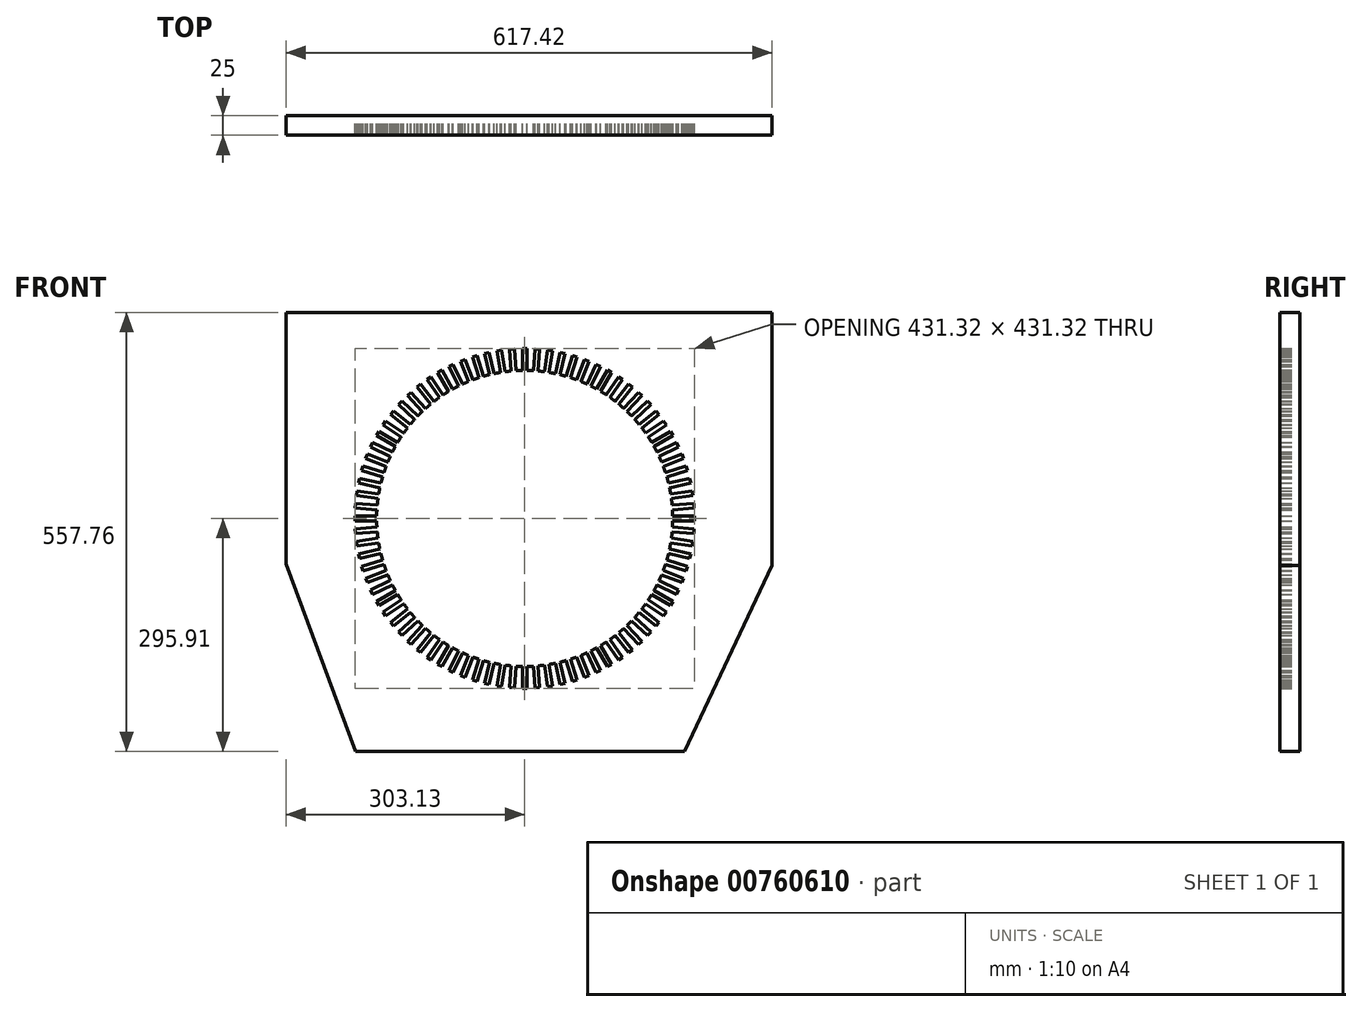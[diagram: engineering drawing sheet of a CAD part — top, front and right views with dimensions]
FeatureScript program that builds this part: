
annotation { "Feature Type Name" : "Feature", "Feature Type Description" : "" }
export const myFeature = defineFeature(function(context is Context, id is Id, definition is map)
    precondition{}
    {
        {
            var Q0;
            Q0=qCreatedBy(makeId("Front.planeOp"),FACE);
            var sketch = newSketch(context, id + "F0", { "sketchPlane" : qUnion([Q0])});
            skCircle(sketch, "E0", {"center": v(0, 0) * mm, "radius": 188.04 * mm});
            skLineSegment(sketch, "E1.top", {"start": v(3, 215.66) * mm, "end": v(-3, 215.66) * mm});
            skLineSegment(sketch, "E1.left", {"start": v(3, 185.67) * mm, "end": v(3, 215.66) * mm});
            skLineSegment(sketch, "E1.right", {"start": v(-3, 185.67) * mm, "end": v(-3, 215.66) * mm});
            skPoint(sketch, "E1.middle", {"position": v(0, 200.67) * mm});
            skLineSegment(sketch, "E2", {"start": v(0, 184.62) * mm, "end": v(0, -162.33) * mm, "construction": true});
            skLineSegment(sketch, "E3.1.0", {"start": v(-10.88, 185.38) * mm, "end": v(-13.12, 215.28) * mm});
            skLineSegment(sketch, "E3.1.1", {"start": v(-16.87, 184.93) * mm, "end": v(-19.1, 214.83) * mm});
            skPoint(sketch, "E3.1.2", {"position": v(-15, 200.1) * mm});
            skLineSegment(sketch, "E3.1.3", {"start": v(-13.12, 215.28) * mm, "end": v(-19.1, 214.83) * mm});
            skLineSegment(sketch, "E3.2.0", {"start": v(-24.7, 184.05) * mm, "end": v(-29.18, 213.7) * mm});
            skLineSegment(sketch, "E3.2.1", {"start": v(-30.64, 183.15) * mm, "end": v(-35.1, 212.8) * mm});
            skPoint(sketch, "E3.2.2", {"position": v(-29.9, 198.43) * mm});
            skLineSegment(sketch, "E3.2.3", {"start": v(-29.18, 213.7) * mm, "end": v(-35.1, 212.8) * mm});
            skLineSegment(sketch, "E3.3.0", {"start": v(-38.4, 181.69) * mm, "end": v(-45.06, 210.92) * mm});
            skLineSegment(sketch, "E3.3.1", {"start": v(-44.24, 180.35) * mm, "end": v(-50.91, 209.59) * mm});
            skPoint(sketch, "E3.3.2", {"position": v(-44.65, 195.64) * mm});
            skLineSegment(sketch, "E3.3.3", {"start": v(-45.06, 210.92) * mm, "end": v(-50.91, 209.59) * mm});
            skLineSegment(sketch, "E3.4.0", {"start": v(-51.86, 178.3) * mm, "end": v(-60.7, 206.96) * mm});
            skLineSegment(sketch, "E3.4.1", {"start": v(-57.6, 176.54) * mm, "end": v(-66.43, 205.2) * mm});
            skPoint(sketch, "E3.4.2", {"position": v(-59.15, 191.75) * mm});
            skLineSegment(sketch, "E3.4.3", {"start": v(-60.7, 206.96) * mm, "end": v(-66.43, 205.2) * mm});
            skLineSegment(sketch, "E3.5.0", {"start": v(-65.04, 173.93) * mm, "end": v(-76, 201.85) * mm});
            skLineSegment(sketch, "E3.5.1", {"start": v(-70.63, 171.74) * mm, "end": v(-81.58, 199.66) * mm});
            skPoint(sketch, "E3.5.2", {"position": v(-73.31, 186.8) * mm});
            skLineSegment(sketch, "E3.5.3", {"start": v(-76, 201.85) * mm, "end": v(-81.58, 199.66) * mm});
            skLineSegment(sketch, "E3.6.0", {"start": v(-77.86, 168.59) * mm, "end": v(-90.87, 195.6) * mm});
            skLineSegment(sketch, "E3.6.1", {"start": v(-83.26, 165.98) * mm, "end": v(-96.27, 193) * mm});
            skPoint(sketch, "E3.6.2", {"position": v(-87.07, 180.8) * mm});
            skLineSegment(sketch, "E3.6.3", {"start": v(-90.87, 195.6) * mm, "end": v(-96.27, 193) * mm});
            skLineSegment(sketch, "E3.7.0", {"start": v(-90.24, 162.3) * mm, "end": v(-105.23, 188.27) * mm});
            skLineSegment(sketch, "E3.7.1", {"start": v(-95.43, 159.3) * mm, "end": v(-110.43, 185.27) * mm});
            skPoint(sketch, "E3.7.2", {"position": v(-100.33, 173.78) * mm});
            skLineSegment(sketch, "E3.7.3", {"start": v(-105.23, 188.27) * mm, "end": v(-110.43, 185.27) * mm});
            skLineSegment(sketch, "E3.8.0", {"start": v(-102.11, 155.1) * mm, "end": v(-119, 179.88) * mm});
            skLineSegment(sketch, "E3.8.1", {"start": v(-107.07, 151.72) * mm, "end": v(-123.96, 176.5) * mm});
            skPoint(sketch, "E3.8.2", {"position": v(-113.04, 165.8) * mm});
            skLineSegment(sketch, "E3.8.3", {"start": v(-119, 179.88) * mm, "end": v(-123.96, 176.5) * mm});
            skLineSegment(sketch, "E3.9.0", {"start": v(-113.42, 147.04) * mm, "end": v(-132.12, 170.48) * mm});
            skLineSegment(sketch, "E3.9.1", {"start": v(-118.11, 143.3) * mm, "end": v(-136.8, 166.74) * mm});
            skPoint(sketch, "E3.9.2", {"position": v(-125.11, 156.89) * mm});
            skLineSegment(sketch, "E3.9.3", {"start": v(-132.12, 170.48) * mm, "end": v(-136.8, 166.74) * mm});
            skLineSegment(sketch, "E3.10.0", {"start": v(-124.1, 138.15) * mm, "end": v(-144.49, 160.13) * mm});
            skLineSegment(sketch, "E3.10.1", {"start": v(-128.49, 134.07) * mm, "end": v(-148.89, 156.05) * mm});
            skPoint(sketch, "E3.10.2", {"position": v(-136.49, 147.1) * mm});
            skLineSegment(sketch, "E3.10.3", {"start": v(-144.49, 160.13) * mm, "end": v(-148.89, 156.05) * mm});
            skLineSegment(sketch, "E3.11.0", {"start": v(-134.07, 128.49) * mm, "end": v(-156.05, 148.89) * mm});
            skLineSegment(sketch, "E3.11.1", {"start": v(-138.15, 124.1) * mm, "end": v(-160.13, 144.49) * mm});
            skPoint(sketch, "E3.11.2", {"position": v(-147.1, 136.49) * mm});
            skLineSegment(sketch, "E3.11.3", {"start": v(-156.05, 148.89) * mm, "end": v(-160.13, 144.49) * mm});
            skLineSegment(sketch, "E3.12.0", {"start": v(-143.3, 118.11) * mm, "end": v(-166.74, 136.8) * mm});
            skLineSegment(sketch, "E3.12.1", {"start": v(-147.04, 113.42) * mm, "end": v(-170.48, 132.12) * mm});
            skPoint(sketch, "E3.12.2", {"position": v(-156.89, 125.11) * mm});
            skLineSegment(sketch, "E3.12.3", {"start": v(-166.74, 136.8) * mm, "end": v(-170.48, 132.12) * mm});
            skLineSegment(sketch, "E3.13.0", {"start": v(-151.72, 107.07) * mm, "end": v(-176.5, 123.96) * mm});
            skLineSegment(sketch, "E3.13.1", {"start": v(-155.1, 102.11) * mm, "end": v(-179.88, 119) * mm});
            skPoint(sketch, "E3.13.2", {"position": v(-165.8, 113.04) * mm});
            skLineSegment(sketch, "E3.13.3", {"start": v(-176.5, 123.96) * mm, "end": v(-179.88, 119) * mm});
            skLineSegment(sketch, "E3.14.0", {"start": v(-159.3, 95.43) * mm, "end": v(-185.27, 110.43) * mm});
            skLineSegment(sketch, "E3.14.1", {"start": v(-162.3, 90.24) * mm, "end": v(-188.27, 105.23) * mm});
            skPoint(sketch, "E3.14.2", {"position": v(-173.78, 100.33) * mm});
            skLineSegment(sketch, "E3.14.3", {"start": v(-185.27, 110.43) * mm, "end": v(-188.27, 105.23) * mm});
            skLineSegment(sketch, "E3.15.0", {"start": v(-165.98, 83.26) * mm, "end": v(-193, 96.27) * mm});
            skLineSegment(sketch, "E3.15.1", {"start": v(-168.59, 77.86) * mm, "end": v(-195.6, 90.87) * mm});
            skPoint(sketch, "E3.15.2", {"position": v(-180.8, 87.07) * mm});
            skLineSegment(sketch, "E3.15.3", {"start": v(-193, 96.27) * mm, "end": v(-195.6, 90.87) * mm});
            skLineSegment(sketch, "E3.16.0", {"start": v(-171.74, 70.63) * mm, "end": v(-199.66, 81.58) * mm});
            skLineSegment(sketch, "E3.16.1", {"start": v(-173.93, 65.04) * mm, "end": v(-201.85, 76) * mm});
            skPoint(sketch, "E3.16.2", {"position": v(-186.8, 73.31) * mm});
            skLineSegment(sketch, "E3.16.3", {"start": v(-199.66, 81.58) * mm, "end": v(-201.85, 76) * mm});
            skLineSegment(sketch, "E3.17.0", {"start": v(-176.54, 57.6) * mm, "end": v(-205.2, 66.43) * mm});
            skLineSegment(sketch, "E3.17.1", {"start": v(-178.3, 51.86) * mm, "end": v(-206.96, 60.7) * mm});
            skPoint(sketch, "E3.17.2", {"position": v(-191.75, 59.15) * mm});
            skLineSegment(sketch, "E3.17.3", {"start": v(-205.2, 66.43) * mm, "end": v(-206.96, 60.7) * mm});
            skLineSegment(sketch, "E3.18.0", {"start": v(-180.35, 44.24) * mm, "end": v(-209.59, 50.91) * mm});
            skLineSegment(sketch, "E3.18.1", {"start": v(-181.69, 38.4) * mm, "end": v(-210.92, 45.06) * mm});
            skPoint(sketch, "E3.18.2", {"position": v(-195.64, 44.65) * mm});
            skLineSegment(sketch, "E3.18.3", {"start": v(-209.59, 50.91) * mm, "end": v(-210.92, 45.06) * mm});
            skLineSegment(sketch, "E3.19.0", {"start": v(-183.15, 30.64) * mm, "end": v(-212.8, 35.1) * mm});
            skLineSegment(sketch, "E3.19.1", {"start": v(-184.05, 24.7) * mm, "end": v(-213.7, 29.18) * mm});
            skPoint(sketch, "E3.19.2", {"position": v(-198.43, 29.9) * mm});
            skLineSegment(sketch, "E3.19.3", {"start": v(-212.8, 35.1) * mm, "end": v(-213.7, 29.18) * mm});
            skLineSegment(sketch, "E3.20.0", {"start": v(-184.93, 16.87) * mm, "end": v(-214.83, 19.1) * mm});
            skLineSegment(sketch, "E3.20.1", {"start": v(-185.38, 10.88) * mm, "end": v(-215.28, 13.12) * mm});
            skPoint(sketch, "E3.20.2", {"position": v(-200.1, 15) * mm});
            skLineSegment(sketch, "E3.20.3", {"start": v(-214.83, 19.1) * mm, "end": v(-215.28, 13.12) * mm});
            skLineSegment(sketch, "E3.21.0", {"start": v(-185.67, 3) * mm, "end": v(-215.66, 3) * mm});
            skLineSegment(sketch, "E3.21.1", {"start": v(-185.67, -3) * mm, "end": v(-215.66, -3) * mm});
            skPoint(sketch, "E3.21.2", {"position": v(-200.67, 0) * mm});
            skLineSegment(sketch, "E3.21.3", {"start": v(-215.66, 3) * mm, "end": v(-215.66, -3) * mm});
            skLineSegment(sketch, "E3.22.0", {"start": v(-185.38, -10.88) * mm, "end": v(-215.28, -13.12) * mm});
            skLineSegment(sketch, "E3.22.1", {"start": v(-184.93, -16.87) * mm, "end": v(-214.83, -19.1) * mm});
            skPoint(sketch, "E3.22.2", {"position": v(-200.1, -15) * mm});
            skLineSegment(sketch, "E3.22.3", {"start": v(-215.28, -13.12) * mm, "end": v(-214.83, -19.1) * mm});
            skLineSegment(sketch, "E3.23.0", {"start": v(-184.05, -24.7) * mm, "end": v(-213.7, -29.18) * mm});
            skLineSegment(sketch, "E3.23.1", {"start": v(-183.15, -30.64) * mm, "end": v(-212.8, -35.1) * mm});
            skPoint(sketch, "E3.23.2", {"position": v(-198.43, -29.9) * mm});
            skLineSegment(sketch, "E3.23.3", {"start": v(-213.7, -29.18) * mm, "end": v(-212.8, -35.1) * mm});
            skLineSegment(sketch, "E3.24.0", {"start": v(-181.69, -38.4) * mm, "end": v(-210.92, -45.06) * mm});
            skLineSegment(sketch, "E3.24.1", {"start": v(-180.35, -44.24) * mm, "end": v(-209.59, -50.91) * mm});
            skPoint(sketch, "E3.24.2", {"position": v(-195.64, -44.65) * mm});
            skLineSegment(sketch, "E3.24.3", {"start": v(-210.92, -45.06) * mm, "end": v(-209.59, -50.91) * mm});
            skLineSegment(sketch, "E3.25.0", {"start": v(-178.3, -51.86) * mm, "end": v(-206.96, -60.7) * mm});
            skLineSegment(sketch, "E3.25.1", {"start": v(-176.54, -57.6) * mm, "end": v(-205.2, -66.43) * mm});
            skPoint(sketch, "E3.25.2", {"position": v(-191.75, -59.15) * mm});
            skLineSegment(sketch, "E3.25.3", {"start": v(-206.96, -60.7) * mm, "end": v(-205.2, -66.43) * mm});
            skLineSegment(sketch, "E3.26.0", {"start": v(-173.93, -65.04) * mm, "end": v(-201.85, -76) * mm});
            skLineSegment(sketch, "E3.26.1", {"start": v(-171.74, -70.63) * mm, "end": v(-199.66, -81.58) * mm});
            skPoint(sketch, "E3.26.2", {"position": v(-186.8, -73.31) * mm});
            skLineSegment(sketch, "E3.26.3", {"start": v(-201.85, -76) * mm, "end": v(-199.66, -81.58) * mm});
            skLineSegment(sketch, "E3.27.0", {"start": v(-168.59, -77.86) * mm, "end": v(-195.6, -90.87) * mm});
            skLineSegment(sketch, "E3.27.1", {"start": v(-165.98, -83.26) * mm, "end": v(-193, -96.27) * mm});
            skPoint(sketch, "E3.27.2", {"position": v(-180.8, -87.07) * mm});
            skLineSegment(sketch, "E3.27.3", {"start": v(-195.6, -90.87) * mm, "end": v(-193, -96.27) * mm});
            skLineSegment(sketch, "E3.28.0", {"start": v(-162.3, -90.24) * mm, "end": v(-188.27, -105.23) * mm});
            skLineSegment(sketch, "E3.28.1", {"start": v(-159.3, -95.43) * mm, "end": v(-185.27, -110.43) * mm});
            skPoint(sketch, "E3.28.2", {"position": v(-173.78, -100.33) * mm});
            skLineSegment(sketch, "E3.28.3", {"start": v(-188.27, -105.23) * mm, "end": v(-185.27, -110.43) * mm});
            skLineSegment(sketch, "E3.29.0", {"start": v(-155.1, -102.11) * mm, "end": v(-179.88, -119) * mm});
            skLineSegment(sketch, "E3.29.1", {"start": v(-151.72, -107.07) * mm, "end": v(-176.5, -123.96) * mm});
            skPoint(sketch, "E3.29.2", {"position": v(-165.8, -113.04) * mm});
            skLineSegment(sketch, "E3.29.3", {"start": v(-179.88, -119) * mm, "end": v(-176.5, -123.96) * mm});
            skLineSegment(sketch, "E3.30.0", {"start": v(-147.04, -113.42) * mm, "end": v(-170.48, -132.12) * mm});
            skLineSegment(sketch, "E3.30.1", {"start": v(-143.3, -118.11) * mm, "end": v(-166.74, -136.8) * mm});
            skPoint(sketch, "E3.30.2", {"position": v(-156.89, -125.11) * mm});
            skLineSegment(sketch, "E3.30.3", {"start": v(-170.48, -132.12) * mm, "end": v(-166.74, -136.8) * mm});
            skLineSegment(sketch, "E3.31.0", {"start": v(-138.15, -124.1) * mm, "end": v(-160.13, -144.49) * mm});
            skLineSegment(sketch, "E3.31.1", {"start": v(-134.07, -128.49) * mm, "end": v(-156.05, -148.89) * mm});
            skPoint(sketch, "E3.31.2", {"position": v(-147.1, -136.49) * mm});
            skLineSegment(sketch, "E3.31.3", {"start": v(-160.13, -144.49) * mm, "end": v(-156.05, -148.89) * mm});
            skLineSegment(sketch, "E3.32.0", {"start": v(-128.49, -134.07) * mm, "end": v(-148.89, -156.05) * mm});
            skLineSegment(sketch, "E3.32.1", {"start": v(-124.1, -138.15) * mm, "end": v(-144.49, -160.13) * mm});
            skPoint(sketch, "E3.32.2", {"position": v(-136.49, -147.1) * mm});
            skLineSegment(sketch, "E3.32.3", {"start": v(-148.89, -156.05) * mm, "end": v(-144.49, -160.13) * mm});
            skLineSegment(sketch, "E3.33.0", {"start": v(-118.11, -143.3) * mm, "end": v(-136.8, -166.74) * mm});
            skLineSegment(sketch, "E3.33.1", {"start": v(-113.42, -147.04) * mm, "end": v(-132.12, -170.48) * mm});
            skPoint(sketch, "E3.33.2", {"position": v(-125.11, -156.89) * mm});
            skLineSegment(sketch, "E3.33.3", {"start": v(-136.8, -166.74) * mm, "end": v(-132.12, -170.48) * mm});
            skLineSegment(sketch, "E3.34.0", {"start": v(-107.07, -151.72) * mm, "end": v(-123.96, -176.5) * mm});
            skLineSegment(sketch, "E3.34.1", {"start": v(-102.11, -155.1) * mm, "end": v(-119, -179.88) * mm});
            skPoint(sketch, "E3.34.2", {"position": v(-113.04, -165.8) * mm});
            skLineSegment(sketch, "E3.34.3", {"start": v(-123.96, -176.5) * mm, "end": v(-119, -179.88) * mm});
            skLineSegment(sketch, "E3.35.0", {"start": v(-95.43, -159.3) * mm, "end": v(-110.43, -185.27) * mm});
            skLineSegment(sketch, "E3.35.1", {"start": v(-90.24, -162.3) * mm, "end": v(-105.23, -188.27) * mm});
            skPoint(sketch, "E3.35.2", {"position": v(-100.33, -173.78) * mm});
            skLineSegment(sketch, "E3.35.3", {"start": v(-110.43, -185.27) * mm, "end": v(-105.23, -188.27) * mm});
            skLineSegment(sketch, "E3.36.0", {"start": v(-83.26, -165.98) * mm, "end": v(-96.27, -193) * mm});
            skLineSegment(sketch, "E3.36.1", {"start": v(-77.86, -168.59) * mm, "end": v(-90.87, -195.6) * mm});
            skPoint(sketch, "E3.36.2", {"position": v(-87.07, -180.8) * mm});
            skLineSegment(sketch, "E3.36.3", {"start": v(-96.27, -193) * mm, "end": v(-90.87, -195.6) * mm});
            skLineSegment(sketch, "E3.37.0", {"start": v(-70.63, -171.74) * mm, "end": v(-81.58, -199.66) * mm});
            skLineSegment(sketch, "E3.37.1", {"start": v(-65.04, -173.93) * mm, "end": v(-76, -201.85) * mm});
            skPoint(sketch, "E3.37.2", {"position": v(-73.31, -186.8) * mm});
            skLineSegment(sketch, "E3.37.3", {"start": v(-81.58, -199.66) * mm, "end": v(-76, -201.85) * mm});
            skLineSegment(sketch, "E3.38.0", {"start": v(-57.6, -176.54) * mm, "end": v(-66.43, -205.2) * mm});
            skLineSegment(sketch, "E3.38.1", {"start": v(-51.86, -178.3) * mm, "end": v(-60.7, -206.96) * mm});
            skPoint(sketch, "E3.38.2", {"position": v(-59.15, -191.75) * mm});
            skLineSegment(sketch, "E3.38.3", {"start": v(-66.43, -205.2) * mm, "end": v(-60.7, -206.96) * mm});
            skLineSegment(sketch, "E3.39.0", {"start": v(-44.24, -180.35) * mm, "end": v(-50.91, -209.59) * mm});
            skLineSegment(sketch, "E3.39.1", {"start": v(-38.4, -181.69) * mm, "end": v(-45.06, -210.92) * mm});
            skPoint(sketch, "E3.39.2", {"position": v(-44.65, -195.64) * mm});
            skLineSegment(sketch, "E3.39.3", {"start": v(-50.91, -209.59) * mm, "end": v(-45.06, -210.92) * mm});
            skLineSegment(sketch, "E3.40.0", {"start": v(-30.64, -183.15) * mm, "end": v(-35.1, -212.8) * mm});
            skLineSegment(sketch, "E3.40.1", {"start": v(-24.7, -184.05) * mm, "end": v(-29.18, -213.7) * mm});
            skPoint(sketch, "E3.40.2", {"position": v(-29.9, -198.43) * mm});
            skLineSegment(sketch, "E3.40.3", {"start": v(-35.1, -212.8) * mm, "end": v(-29.18, -213.7) * mm});
            skLineSegment(sketch, "E3.41.0", {"start": v(-16.87, -184.93) * mm, "end": v(-19.1, -214.83) * mm});
            skLineSegment(sketch, "E3.41.1", {"start": v(-10.88, -185.38) * mm, "end": v(-13.12, -215.28) * mm});
            skPoint(sketch, "E3.41.2", {"position": v(-15, -200.1) * mm});
            skLineSegment(sketch, "E3.41.3", {"start": v(-19.1, -214.83) * mm, "end": v(-13.12, -215.28) * mm});
            skLineSegment(sketch, "E3.42.0", {"start": v(-3, -185.67) * mm, "end": v(-3, -215.66) * mm});
            skLineSegment(sketch, "E3.42.1", {"start": v(3, -185.67) * mm, "end": v(3, -215.66) * mm});
            skPoint(sketch, "E3.42.2", {"position": v(0, -200.67) * mm});
            skLineSegment(sketch, "E3.42.3", {"start": v(-3, -215.66) * mm, "end": v(3, -215.66) * mm});
            skLineSegment(sketch, "E3.43.0", {"start": v(10.88, -185.38) * mm, "end": v(13.12, -215.28) * mm});
            skLineSegment(sketch, "E3.43.1", {"start": v(16.87, -184.93) * mm, "end": v(19.1, -214.83) * mm});
            skPoint(sketch, "E3.43.2", {"position": v(15, -200.1) * mm});
            skLineSegment(sketch, "E3.43.3", {"start": v(13.12, -215.28) * mm, "end": v(19.1, -214.83) * mm});
            skLineSegment(sketch, "E3.44.0", {"start": v(24.7, -184.05) * mm, "end": v(29.18, -213.7) * mm});
            skLineSegment(sketch, "E3.44.1", {"start": v(30.64, -183.15) * mm, "end": v(35.1, -212.8) * mm});
            skPoint(sketch, "E3.44.2", {"position": v(29.9, -198.43) * mm});
            skLineSegment(sketch, "E3.44.3", {"start": v(29.18, -213.7) * mm, "end": v(35.1, -212.8) * mm});
            skLineSegment(sketch, "E3.45.0", {"start": v(38.4, -181.69) * mm, "end": v(45.06, -210.92) * mm});
            skLineSegment(sketch, "E3.45.1", {"start": v(44.24, -180.35) * mm, "end": v(50.91, -209.59) * mm});
            skPoint(sketch, "E3.45.2", {"position": v(44.65, -195.64) * mm});
            skLineSegment(sketch, "E3.45.3", {"start": v(45.06, -210.92) * mm, "end": v(50.91, -209.59) * mm});
            skLineSegment(sketch, "E3.46.0", {"start": v(51.86, -178.3) * mm, "end": v(60.7, -206.96) * mm});
            skLineSegment(sketch, "E3.46.1", {"start": v(57.6, -176.54) * mm, "end": v(66.43, -205.2) * mm});
            skPoint(sketch, "E3.46.2", {"position": v(59.15, -191.75) * mm});
            skLineSegment(sketch, "E3.46.3", {"start": v(60.7, -206.96) * mm, "end": v(66.43, -205.2) * mm});
            skLineSegment(sketch, "E3.47.0", {"start": v(65.04, -173.93) * mm, "end": v(76, -201.85) * mm});
            skLineSegment(sketch, "E3.47.1", {"start": v(70.63, -171.74) * mm, "end": v(81.58, -199.66) * mm});
            skPoint(sketch, "E3.47.2", {"position": v(73.31, -186.8) * mm});
            skLineSegment(sketch, "E3.47.3", {"start": v(76, -201.85) * mm, "end": v(81.58, -199.66) * mm});
            skLineSegment(sketch, "E3.48.0", {"start": v(77.86, -168.59) * mm, "end": v(90.87, -195.6) * mm});
            skLineSegment(sketch, "E3.48.1", {"start": v(83.26, -165.98) * mm, "end": v(96.27, -193) * mm});
            skPoint(sketch, "E3.48.2", {"position": v(87.07, -180.8) * mm});
            skLineSegment(sketch, "E3.48.3", {"start": v(90.87, -195.6) * mm, "end": v(96.27, -193) * mm});
            skLineSegment(sketch, "E3.49.0", {"start": v(90.24, -162.3) * mm, "end": v(105.23, -188.27) * mm});
            skLineSegment(sketch, "E3.49.1", {"start": v(95.43, -159.3) * mm, "end": v(110.43, -185.27) * mm});
            skPoint(sketch, "E3.49.2", {"position": v(100.33, -173.78) * mm});
            skLineSegment(sketch, "E3.49.3", {"start": v(105.23, -188.27) * mm, "end": v(110.43, -185.27) * mm});
            skLineSegment(sketch, "E3.50.0", {"start": v(102.11, -155.1) * mm, "end": v(119, -179.88) * mm});
            skLineSegment(sketch, "E3.50.1", {"start": v(107.07, -151.72) * mm, "end": v(123.96, -176.5) * mm});
            skPoint(sketch, "E3.50.2", {"position": v(113.04, -165.8) * mm});
            skLineSegment(sketch, "E3.50.3", {"start": v(119, -179.88) * mm, "end": v(123.96, -176.5) * mm});
            skLineSegment(sketch, "E3.51.0", {"start": v(113.42, -147.04) * mm, "end": v(132.12, -170.48) * mm});
            skLineSegment(sketch, "E3.51.1", {"start": v(118.11, -143.3) * mm, "end": v(136.8, -166.74) * mm});
            skPoint(sketch, "E3.51.2", {"position": v(125.11, -156.89) * mm});
            skLineSegment(sketch, "E3.51.3", {"start": v(132.12, -170.48) * mm, "end": v(136.8, -166.74) * mm});
            skLineSegment(sketch, "E3.52.0", {"start": v(124.1, -138.15) * mm, "end": v(144.49, -160.13) * mm});
            skLineSegment(sketch, "E3.52.1", {"start": v(128.49, -134.07) * mm, "end": v(148.89, -156.05) * mm});
            skPoint(sketch, "E3.52.2", {"position": v(136.49, -147.1) * mm});
            skLineSegment(sketch, "E3.52.3", {"start": v(144.49, -160.13) * mm, "end": v(148.89, -156.05) * mm});
            skLineSegment(sketch, "E3.53.0", {"start": v(134.07, -128.49) * mm, "end": v(156.05, -148.89) * mm});
            skLineSegment(sketch, "E3.53.1", {"start": v(138.15, -124.1) * mm, "end": v(160.13, -144.49) * mm});
            skPoint(sketch, "E3.53.2", {"position": v(147.1, -136.49) * mm});
            skLineSegment(sketch, "E3.53.3", {"start": v(156.05, -148.89) * mm, "end": v(160.13, -144.49) * mm});
            skLineSegment(sketch, "E3.54.0", {"start": v(143.3, -118.11) * mm, "end": v(166.74, -136.8) * mm});
            skLineSegment(sketch, "E3.54.1", {"start": v(147.04, -113.42) * mm, "end": v(170.48, -132.12) * mm});
            skPoint(sketch, "E3.54.2", {"position": v(156.89, -125.11) * mm});
            skLineSegment(sketch, "E3.54.3", {"start": v(166.74, -136.8) * mm, "end": v(170.48, -132.12) * mm});
            skLineSegment(sketch, "E3.55.0", {"start": v(151.72, -107.07) * mm, "end": v(176.5, -123.96) * mm});
            skLineSegment(sketch, "E3.55.1", {"start": v(155.1, -102.11) * mm, "end": v(179.88, -119) * mm});
            skPoint(sketch, "E3.55.2", {"position": v(165.8, -113.04) * mm});
            skLineSegment(sketch, "E3.55.3", {"start": v(176.5, -123.96) * mm, "end": v(179.88, -119) * mm});
            skLineSegment(sketch, "E3.56.0", {"start": v(159.3, -95.43) * mm, "end": v(185.27, -110.43) * mm});
            skLineSegment(sketch, "E3.56.1", {"start": v(162.3, -90.24) * mm, "end": v(188.27, -105.23) * mm});
            skPoint(sketch, "E3.56.2", {"position": v(173.78, -100.33) * mm});
            skLineSegment(sketch, "E3.56.3", {"start": v(185.27, -110.43) * mm, "end": v(188.27, -105.23) * mm});
            skLineSegment(sketch, "E3.57.0", {"start": v(165.98, -83.26) * mm, "end": v(193, -96.27) * mm});
            skLineSegment(sketch, "E3.57.1", {"start": v(168.59, -77.86) * mm, "end": v(195.6, -90.87) * mm});
            skPoint(sketch, "E3.57.2", {"position": v(180.8, -87.07) * mm});
            skLineSegment(sketch, "E3.57.3", {"start": v(193, -96.27) * mm, "end": v(195.6, -90.87) * mm});
            skLineSegment(sketch, "E3.58.0", {"start": v(171.74, -70.63) * mm, "end": v(199.66, -81.58) * mm});
            skLineSegment(sketch, "E3.58.1", {"start": v(173.93, -65.04) * mm, "end": v(201.85, -76) * mm});
            skPoint(sketch, "E3.58.2", {"position": v(186.8, -73.31) * mm});
            skLineSegment(sketch, "E3.58.3", {"start": v(199.66, -81.58) * mm, "end": v(201.85, -76) * mm});
            skLineSegment(sketch, "E3.59.0", {"start": v(176.54, -57.6) * mm, "end": v(205.2, -66.43) * mm});
            skLineSegment(sketch, "E3.59.1", {"start": v(178.3, -51.86) * mm, "end": v(206.96, -60.7) * mm});
            skPoint(sketch, "E3.59.2", {"position": v(191.75, -59.15) * mm});
            skLineSegment(sketch, "E3.59.3", {"start": v(205.2, -66.43) * mm, "end": v(206.96, -60.7) * mm});
            skLineSegment(sketch, "E3.60.0", {"start": v(180.35, -44.24) * mm, "end": v(209.59, -50.91) * mm});
            skLineSegment(sketch, "E3.60.1", {"start": v(181.69, -38.4) * mm, "end": v(210.92, -45.06) * mm});
            skPoint(sketch, "E3.60.2", {"position": v(195.64, -44.65) * mm});
            skLineSegment(sketch, "E3.60.3", {"start": v(209.59, -50.91) * mm, "end": v(210.92, -45.06) * mm});
            skLineSegment(sketch, "E3.61.0", {"start": v(183.15, -30.64) * mm, "end": v(212.8, -35.1) * mm});
            skLineSegment(sketch, "E3.61.1", {"start": v(184.05, -24.7) * mm, "end": v(213.7, -29.18) * mm});
            skPoint(sketch, "E3.61.2", {"position": v(198.43, -29.9) * mm});
            skLineSegment(sketch, "E3.61.3", {"start": v(212.8, -35.1) * mm, "end": v(213.7, -29.18) * mm});
            skLineSegment(sketch, "E3.62.0", {"start": v(184.93, -16.87) * mm, "end": v(214.83, -19.1) * mm});
            skLineSegment(sketch, "E3.62.1", {"start": v(185.38, -10.88) * mm, "end": v(215.28, -13.12) * mm});
            skPoint(sketch, "E3.62.2", {"position": v(200.1, -15) * mm});
            skLineSegment(sketch, "E3.62.3", {"start": v(214.83, -19.1) * mm, "end": v(215.28, -13.12) * mm});
            skLineSegment(sketch, "E3.63.0", {"start": v(185.67, -3) * mm, "end": v(215.66, -3) * mm});
            skLineSegment(sketch, "E3.63.1", {"start": v(185.67, 3) * mm, "end": v(215.66, 3) * mm});
            skPoint(sketch, "E3.63.2", {"position": v(200.67, 0) * mm});
            skLineSegment(sketch, "E3.63.3", {"start": v(215.66, -3) * mm, "end": v(215.66, 3) * mm});
            skLineSegment(sketch, "E3.64.0", {"start": v(185.38, 10.88) * mm, "end": v(215.28, 13.12) * mm});
            skLineSegment(sketch, "E3.64.1", {"start": v(184.93, 16.87) * mm, "end": v(214.83, 19.1) * mm});
            skPoint(sketch, "E3.64.2", {"position": v(200.1, 15) * mm});
            skLineSegment(sketch, "E3.64.3", {"start": v(215.28, 13.12) * mm, "end": v(214.83, 19.1) * mm});
            skLineSegment(sketch, "E3.65.0", {"start": v(184.05, 24.7) * mm, "end": v(213.7, 29.18) * mm});
            skLineSegment(sketch, "E3.65.1", {"start": v(183.15, 30.64) * mm, "end": v(212.8, 35.1) * mm});
            skPoint(sketch, "E3.65.2", {"position": v(198.43, 29.9) * mm});
            skLineSegment(sketch, "E3.65.3", {"start": v(213.7, 29.18) * mm, "end": v(212.8, 35.1) * mm});
            skLineSegment(sketch, "E3.66.0", {"start": v(181.69, 38.4) * mm, "end": v(210.92, 45.06) * mm});
            skLineSegment(sketch, "E3.66.1", {"start": v(180.35, 44.24) * mm, "end": v(209.59, 50.91) * mm});
            skPoint(sketch, "E3.66.2", {"position": v(195.64, 44.65) * mm});
            skLineSegment(sketch, "E3.66.3", {"start": v(210.92, 45.06) * mm, "end": v(209.59, 50.91) * mm});
            skLineSegment(sketch, "E3.67.0", {"start": v(178.3, 51.86) * mm, "end": v(206.96, 60.7) * mm});
            skLineSegment(sketch, "E3.67.1", {"start": v(176.54, 57.6) * mm, "end": v(205.2, 66.43) * mm});
            skPoint(sketch, "E3.67.2", {"position": v(191.75, 59.15) * mm});
            skLineSegment(sketch, "E3.67.3", {"start": v(206.96, 60.7) * mm, "end": v(205.2, 66.43) * mm});
            skLineSegment(sketch, "E3.68.0", {"start": v(173.93, 65.04) * mm, "end": v(201.85, 76) * mm});
            skLineSegment(sketch, "E3.68.1", {"start": v(171.74, 70.63) * mm, "end": v(199.66, 81.58) * mm});
            skPoint(sketch, "E3.68.2", {"position": v(186.8, 73.31) * mm});
            skLineSegment(sketch, "E3.68.3", {"start": v(201.85, 76) * mm, "end": v(199.66, 81.58) * mm});
            skLineSegment(sketch, "E3.69.0", {"start": v(168.59, 77.86) * mm, "end": v(195.6, 90.87) * mm});
            skLineSegment(sketch, "E3.69.1", {"start": v(165.98, 83.26) * mm, "end": v(193, 96.27) * mm});
            skPoint(sketch, "E3.69.2", {"position": v(180.8, 87.07) * mm});
            skLineSegment(sketch, "E3.69.3", {"start": v(195.6, 90.87) * mm, "end": v(193, 96.27) * mm});
            skLineSegment(sketch, "E3.70.0", {"start": v(162.3, 90.24) * mm, "end": v(188.27, 105.23) * mm});
            skLineSegment(sketch, "E3.70.1", {"start": v(159.3, 95.43) * mm, "end": v(185.27, 110.43) * mm});
            skPoint(sketch, "E3.70.2", {"position": v(173.78, 100.33) * mm});
            skLineSegment(sketch, "E3.70.3", {"start": v(188.27, 105.23) * mm, "end": v(185.27, 110.43) * mm});
            skLineSegment(sketch, "E3.71.0", {"start": v(155.1, 102.11) * mm, "end": v(179.88, 119) * mm});
            skLineSegment(sketch, "E3.71.1", {"start": v(151.72, 107.07) * mm, "end": v(176.5, 123.96) * mm});
            skPoint(sketch, "E3.71.2", {"position": v(165.8, 113.04) * mm});
            skLineSegment(sketch, "E3.71.3", {"start": v(179.88, 119) * mm, "end": v(176.5, 123.96) * mm});
            skLineSegment(sketch, "E3.72.0", {"start": v(147.04, 113.42) * mm, "end": v(170.48, 132.12) * mm});
            skLineSegment(sketch, "E3.72.1", {"start": v(143.3, 118.11) * mm, "end": v(166.74, 136.8) * mm});
            skPoint(sketch, "E3.72.2", {"position": v(156.89, 125.11) * mm});
            skLineSegment(sketch, "E3.72.3", {"start": v(170.48, 132.12) * mm, "end": v(166.74, 136.8) * mm});
            skLineSegment(sketch, "E3.73.0", {"start": v(138.15, 124.1) * mm, "end": v(160.13, 144.49) * mm});
            skLineSegment(sketch, "E3.73.1", {"start": v(134.07, 128.49) * mm, "end": v(156.05, 148.89) * mm});
            skPoint(sketch, "E3.73.2", {"position": v(147.1, 136.49) * mm});
            skLineSegment(sketch, "E3.73.3", {"start": v(160.13, 144.49) * mm, "end": v(156.05, 148.89) * mm});
            skLineSegment(sketch, "E3.74.0", {"start": v(128.49, 134.07) * mm, "end": v(148.89, 156.05) * mm});
            skLineSegment(sketch, "E3.74.1", {"start": v(124.1, 138.15) * mm, "end": v(144.49, 160.13) * mm});
            skPoint(sketch, "E3.74.2", {"position": v(136.49, 147.1) * mm});
            skLineSegment(sketch, "E3.74.3", {"start": v(148.89, 156.05) * mm, "end": v(144.49, 160.13) * mm});
            skLineSegment(sketch, "E3.75.0", {"start": v(118.11, 143.3) * mm, "end": v(136.8, 166.74) * mm});
            skLineSegment(sketch, "E3.75.1", {"start": v(113.42, 147.04) * mm, "end": v(132.12, 170.48) * mm});
            skPoint(sketch, "E3.75.2", {"position": v(125.11, 156.89) * mm});
            skLineSegment(sketch, "E3.75.3", {"start": v(136.8, 166.74) * mm, "end": v(132.12, 170.48) * mm});
            skLineSegment(sketch, "E3.76.0", {"start": v(107.07, 151.72) * mm, "end": v(123.96, 176.5) * mm});
            skLineSegment(sketch, "E3.76.1", {"start": v(102.11, 155.1) * mm, "end": v(119, 179.88) * mm});
            skPoint(sketch, "E3.76.2", {"position": v(113.04, 165.8) * mm});
            skLineSegment(sketch, "E3.76.3", {"start": v(123.96, 176.5) * mm, "end": v(119, 179.88) * mm});
            skLineSegment(sketch, "E3.77.0", {"start": v(95.43, 159.3) * mm, "end": v(110.43, 185.27) * mm});
            skLineSegment(sketch, "E3.77.1", {"start": v(90.24, 162.3) * mm, "end": v(105.23, 188.27) * mm});
            skPoint(sketch, "E3.77.2", {"position": v(100.33, 173.78) * mm});
            skLineSegment(sketch, "E3.77.3", {"start": v(110.43, 185.27) * mm, "end": v(105.23, 188.27) * mm});
            skLineSegment(sketch, "E3.78.0", {"start": v(83.26, 165.98) * mm, "end": v(96.27, 193) * mm});
            skLineSegment(sketch, "E3.78.1", {"start": v(77.86, 168.59) * mm, "end": v(90.87, 195.6) * mm});
            skPoint(sketch, "E3.78.2", {"position": v(87.07, 180.8) * mm});
            skLineSegment(sketch, "E3.78.3", {"start": v(96.27, 193) * mm, "end": v(90.87, 195.6) * mm});
            skLineSegment(sketch, "E3.79.0", {"start": v(70.63, 171.74) * mm, "end": v(81.58, 199.66) * mm});
            skLineSegment(sketch, "E3.79.1", {"start": v(65.04, 173.93) * mm, "end": v(76, 201.85) * mm});
            skPoint(sketch, "E3.79.2", {"position": v(73.31, 186.8) * mm});
            skLineSegment(sketch, "E3.79.3", {"start": v(81.58, 199.66) * mm, "end": v(76, 201.85) * mm});
            skLineSegment(sketch, "E3.80.0", {"start": v(57.6, 176.54) * mm, "end": v(66.43, 205.2) * mm});
            skLineSegment(sketch, "E3.80.1", {"start": v(51.86, 178.3) * mm, "end": v(60.7, 206.96) * mm});
            skPoint(sketch, "E3.80.2", {"position": v(59.15, 191.75) * mm});
            skLineSegment(sketch, "E3.80.3", {"start": v(66.43, 205.2) * mm, "end": v(60.7, 206.96) * mm});
            skLineSegment(sketch, "E3.81.0", {"start": v(44.24, 180.35) * mm, "end": v(50.91, 209.59) * mm});
            skLineSegment(sketch, "E3.81.1", {"start": v(38.4, 181.69) * mm, "end": v(45.06, 210.92) * mm});
            skPoint(sketch, "E3.81.2", {"position": v(44.65, 195.64) * mm});
            skLineSegment(sketch, "E3.81.3", {"start": v(50.91, 209.59) * mm, "end": v(45.06, 210.92) * mm});
            skLineSegment(sketch, "E3.82.0", {"start": v(30.64, 183.15) * mm, "end": v(35.1, 212.8) * mm});
            skLineSegment(sketch, "E3.82.1", {"start": v(24.7, 184.05) * mm, "end": v(29.18, 213.7) * mm});
            skPoint(sketch, "E3.82.2", {"position": v(29.9, 198.43) * mm});
            skLineSegment(sketch, "E3.82.3", {"start": v(35.1, 212.8) * mm, "end": v(29.18, 213.7) * mm});
            skLineSegment(sketch, "E3.83.0", {"start": v(16.87, 184.93) * mm, "end": v(19.1, 214.83) * mm});
            skLineSegment(sketch, "E3.83.1", {"start": v(10.88, 185.38) * mm, "end": v(13.12, 215.28) * mm});
            skPoint(sketch, "E3.83.2", {"position": v(15, 200.1) * mm});
            skLineSegment(sketch, "E3.83.3", {"start": v(19.1, 214.83) * mm, "end": v(13.12, 215.28) * mm});
            skLineSegment(sketch, "E4", {"start": v(0, -295.9) * mm, "end": v(202.74, -295.9) * mm});
            skLineSegment(sketch, "E5", {"start": v(202.74, -295.9) * mm, "end": v(314.3, -59.84) * mm});
            skLineSegment(sketch, "E6", {"start": v(314.3, -59.84) * mm, "end": v(314.3, 261.85) * mm});
            skLineSegment(sketch, "E7", {"start": v(314.3, 261.85) * mm, "end": v(-303.13, 261.85) * mm});
            skLineSegment(sketch, "E8", {"start": v(-303.13, 261.85) * mm, "end": v(-303.13, -57.6) * mm});
            skLineSegment(sketch, "E9", {"start": v(-303.13, -57.6) * mm, "end": v(-214.93, -295.9) * mm});
            skLineSegment(sketch, "E10", {"start": v(-214.93, -295.9) * mm, "end": v(0, -295.9) * mm});
            skSolve(sketch);
        }
        {
            var Q0;
            Q0 = qSketchRegion(id + "F0", true);
            extrude(context, id + "F1", {"entities" : qUnion([Q0]), "depth" : 25 * mm, "offsetDistance" : 25 * mm});
        }
    });
